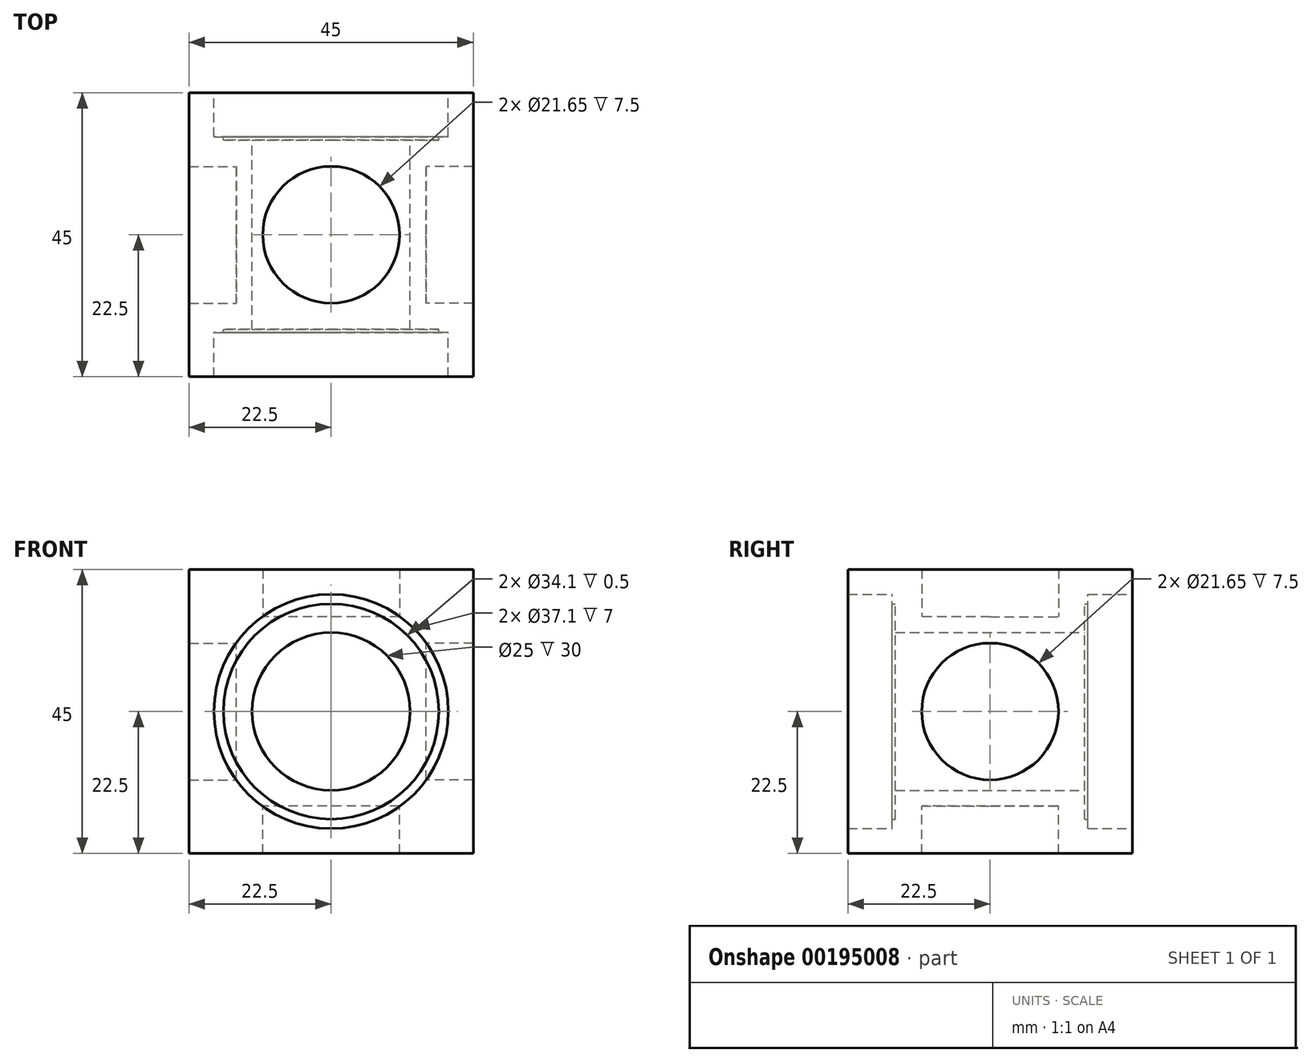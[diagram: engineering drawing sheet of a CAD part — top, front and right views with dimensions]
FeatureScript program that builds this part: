
annotation { "Feature Type Name" : "Feature", "Feature Type Description" : "" }
export const myFeature = defineFeature(function(context is Context, id is Id, definition is map)
    precondition{}
    {
        {
            var Q0;
            Q0=qCreatedBy(makeId("Front.planeOp"),FACE);
            var sketch = newSketch(context, id + "F0", { "sketchPlane" : qUnion([Q0])});
            skLineSegment(sketch, "E0.bottom", {"start": v(22.5, 22.5) * mm, "end": v(-22.5, 22.5) * mm});
            skLineSegment(sketch, "E0.top", {"start": v(22.5, -22.5) * mm, "end": v(-22.5, -22.5) * mm});
            skLineSegment(sketch, "E0.left", {"start": v(22.5, 22.5) * mm, "end": v(22.5, -22.5) * mm});
            skLineSegment(sketch, "E0.right", {"start": v(-22.5, 22.5) * mm, "end": v(-22.5, -22.5) * mm});
            skPoint(sketch, "E0.middle", {"position": v(0, 0) * mm});
            skCircle(sketch, "E1", {"center": v(0, 0) * mm, "radius": 18.55 * mm});
            skCircle(sketch, "E2", {"center": v(0, 0) * mm, "radius": 17.05 * mm});
            skCircle(sketch, "E3", {"center": v(-17.5, 17.5) * mm, "radius": 2 * mm});
            skCircle(sketch, "E4.1.0", {"center": v(-17.5, -17.5) * mm, "radius": 2 * mm});
            skCircle(sketch, "E4.2.0", {"center": v(17.5, -17.5) * mm, "radius": 2 * mm});
            skCircle(sketch, "E4.3.0", {"center": v(17.5, 17.5) * mm, "radius": 2 * mm});
            skCircle(sketch, "E5", {"center": v(0, 0) * mm, "radius": 12.5 * mm});
            skSolve(sketch);
        }
        {
            var Q0;
            Q0=makeQuery(id+"F0.imprint","IMPRINT",FACE,{"disambiguationData":[TD([[makeQuery(id+"F0.imprint","IMPRINT",EDGE,{"derivedFrom":sQuery(id+"F0.wireOp",EDGE,"E0.bottom")}),1.0]])]});
            var Q1;
            Q1=makeQuery(id+"F0.imprint","IMPRINT",FACE,{"disambiguationData":[TD([[makeQuery(id+"F0.imprint","IMPRINT",EDGE,{"derivedFrom":sQuery(id+"F0.wireOp",EDGE,"E3")}),1.0]])]});
            var Q2;
            Q2=makeQuery(id+"F0.imprint","IMPRINT",FACE,{"disambiguationData":[TD([[makeQuery(id+"F0.imprint","IMPRINT",EDGE,{"derivedFrom":sQuery(id+"F0.wireOp",EDGE,"E4.3.0")}),1.0]])]});
            var Q3;
            Q3=makeQuery(id+"F0.imprint","IMPRINT",FACE,{"disambiguationData":[TD([[makeQuery(id+"F0.imprint","IMPRINT",EDGE,{"derivedFrom":sQuery(id+"F0.wireOp",EDGE,"E4.2.0")}),1.0]])]});
            var Q4;
            Q4=makeQuery(id+"F0.imprint","IMPRINT",FACE,{"disambiguationData":[TD([[makeQuery(id+"F0.imprint","IMPRINT",EDGE,{"derivedFrom":sQuery(id+"F0.wireOp",EDGE,"E4.1.0")}),1.0]])]});
            extrude(context, id + "F1", {"entities" : qUnion([Q0, Q1, Q2, Q3, Q4]), "depth" : 45 * mm, "hasSecondDirection" : true, "secondDirectionOppositeDirection" : true, "secondDirectionDepth" : 22.5 * mm, "symmetric" : true});
        }
        {
            var Q0;
            Q0=makeQuery(id+"F0.imprint","IMPRINT",FACE,{"disambiguationData":[TD([[makeQuery(id+"F0.imprint","IMPRINT",EDGE,{"derivedFrom":sQuery(id+"F0.wireOp",EDGE,"E1")}),1.0]])]});
            extrude(context, id + "F2", {"entities" : qUnion([Q0]), "operationType" : NewBodyOperationType.ADD, "depth" : 31 * mm, "symmetric" : true});
        }
        {
            var Q0;
            Q0=qCreatedBy(makeId("Right.planeOp"),FACE);
            var sketch = newSketch(context, id + "F3", { "sketchPlane" : qUnion([Q0])});
            skCircle(sketch, "E6", {"center": v(0, 0) * mm, "radius": 10.82 * mm});
            skLineSegment(sketch, "E7.bottom", {"start": v(-11.25, 11.25) * mm, "end": v(11.25, 11.25) * mm, "construction": true});
            skLineSegment(sketch, "E7.top", {"start": v(-11.25, -11.25) * mm, "end": v(11.25, -11.25) * mm, "construction": true});
            skLineSegment(sketch, "E7.left", {"start": v(-11.25, 11.25) * mm, "end": v(-11.25, -11.25) * mm, "construction": true});
            skLineSegment(sketch, "E7.right", {"start": v(11.25, 11.25) * mm, "end": v(11.25, -11.25) * mm, "construction": true});
            skCircle(sketch, "E8", {"center": v(-11.25, 11.25) * mm, "radius": 2 * mm});
            skCircle(sketch, "E9.1.0", {"center": v(-11.25, -11.25) * mm, "radius": 2 * mm});
            skCircle(sketch, "E9.2.0", {"center": v(11.25, -11.25) * mm, "radius": 2 * mm});
            skCircle(sketch, "E9.3.0", {"center": v(11.25, 11.25) * mm, "radius": 2 * mm});
            skSolve(sketch);
        }
        {
            var Q0;
            Q0=makeQuery(id+"F0.imprint","IMPRINT",FACE,{"disambiguationData":[TD([[makeQuery(id+"F0.imprint","IMPRINT",EDGE,{"derivedFrom":sQuery(id+"F0.wireOp",EDGE,"E2")}),1.0]])]});
            extrude(context, id + "F4", {"entities" : qUnion([Q0]), "operationType" : NewBodyOperationType.ADD, "depth" : 30 * mm, "symmetric" : true});
        }
        {
            var Q0;
            Q0=makeQuery(id+"F3.imprint","IMPRINT",FACE,{"disambiguationData":[TD([[makeQuery(id+"F3.imprint","IMPRINT",EDGE,{"derivedFrom":sQuery(id+"F3.wireOp",EDGE,"E6")}),1.0]])]});
            extrude(context, id + "F5", {"entities" : qUnion([Q0]), "operationType" : NewBodyOperationType.REMOVE, "oppositeDirection" : true, "depth" : 45 * mm, "hasSecondDirection" : true, "secondDirectionOppositeDirection" : true, "secondDirectionDepth" : 15 * mm});
        }
        {
            var Q0;
            Q0=makeQuery(id+"F3.imprint","IMPRINT",FACE,{"disambiguationData":[TD([[makeQuery(id+"F3.imprint","IMPRINT",EDGE,{"derivedFrom":sQuery(id+"F3.wireOp",EDGE,"E6")}),1.0]])]});
            extrude(context, id + "F6", {"entities" : qUnion([Q0]), "operationType" : NewBodyOperationType.REMOVE, "depth" : 45 * mm, "hasSecondDirection" : true, "secondDirectionOppositeDirection" : false, "secondDirectionDepth" : 15 * mm});
        }
        {
            var Q0;
            Q0=qCreatedBy(makeId("Top.planeOp"),FACE);
            var sketch = newSketch(context, id + "F7", { "sketchPlane" : qUnion([Q0])});
            skCircle(sketch, "E10", {"center": v(0, 0) * mm, "radius": 10.82 * mm});
            skSolve(sketch);
        }
        {
            var Q0;
            Q0=makeQuery(id+"F7.imprint","IMPRINT",FACE,{"disambiguationData":[TD([[makeQuery(id+"F7.imprint","IMPRINT",EDGE,{"derivedFrom":sQuery(id+"F7.wireOp",EDGE,"E10")}),1.0]])]});
            extrude(context, id + "F8", {"entities" : qUnion([Q0]), "operationType" : NewBodyOperationType.REMOVE, "depth" : 25 * mm, "hasSecondDirection" : true, "secondDirectionOppositeDirection" : false, "secondDirectionDepth" : 15 * mm});
        }
        {
            var Q0;
            Q0=makeQuery(id+"F7.imprint","IMPRINT",FACE,{"disambiguationData":[TD([[makeQuery(id+"F7.imprint","IMPRINT",EDGE,{"derivedFrom":sQuery(id+"F7.wireOp",EDGE,"E10")}),1.0]])]});
            extrude(context, id + "F9", {"entities" : qUnion([Q0]), "operationType" : NewBodyOperationType.REMOVE, "oppositeDirection" : true, "depth" : 25 * mm, "hasSecondDirection" : true, "secondDirectionOppositeDirection" : true, "secondDirectionDepth" : 15 * mm});
        }
    });
